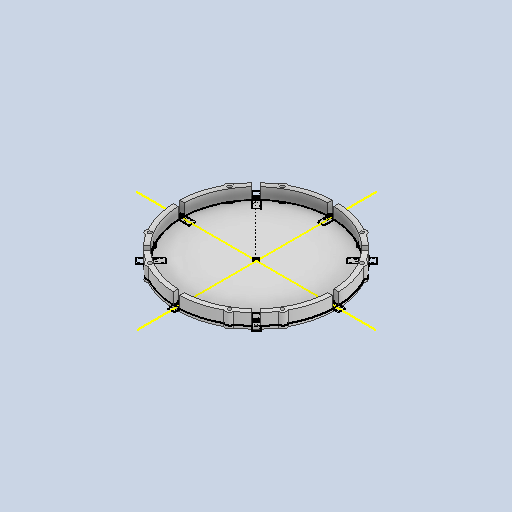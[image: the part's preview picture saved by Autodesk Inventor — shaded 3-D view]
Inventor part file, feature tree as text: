
AUTODESK INVENTOR PART (.ipt)
format: ipt  version: 2024.3 (Build 283343000, 343)  size: 354,816 bytes
history: native  units: in
note: dims shown in document units (in); Inventor stores cm internally (conversion verified against a paired STEP export)
features: extrude x2, sketch x1, hole x1
ambient origin geometry x8: Origin, YZ Plane, XZ Plane, XY Plane, X Axis, Y Axis, Z Axis, Center Point
bodies: Solid1 (feature_tree)
feature tree (4):
  sketch  "Sketch1"  dims[d0=5.5512in d1=5.9055in d4=0.2362in d5=0.7874in d6=3.1496in d8=360.0deg d12=0.1181in d13=0.0in d14=0.9843in d16=0.9843in d21=2.9528in d22=0.9843in d23=0.9843in d24=0.9843in d25=0.9843in d26=2.9528in d27=0.9843in d28=0.9843in d29=2.9528in d30=2.9528in d31=0.315in d32=0.315in d33=0.315in d34=0.315in d35=0.315in d36=0.315in d37=0.315in d38=0.315in d39=0.4134in d40=0.0in d41=0.1378in d42=0.2362in d43=0.1575in d44=0.0787in d45=90.0deg d46=0.315in d47=0.8108in]
  extrude  "Extrusion2"  Depth=0.1575in
  extrude  "Extrusion3"  Depth=0.2362in
  hole  "Hole1"  [1 undecoded]
note: 1 required parameter value undecoded (feature->parameter linkage not recoverable at this tier; creation-order binding heuristic only, values carry confidence <= 0.55)
